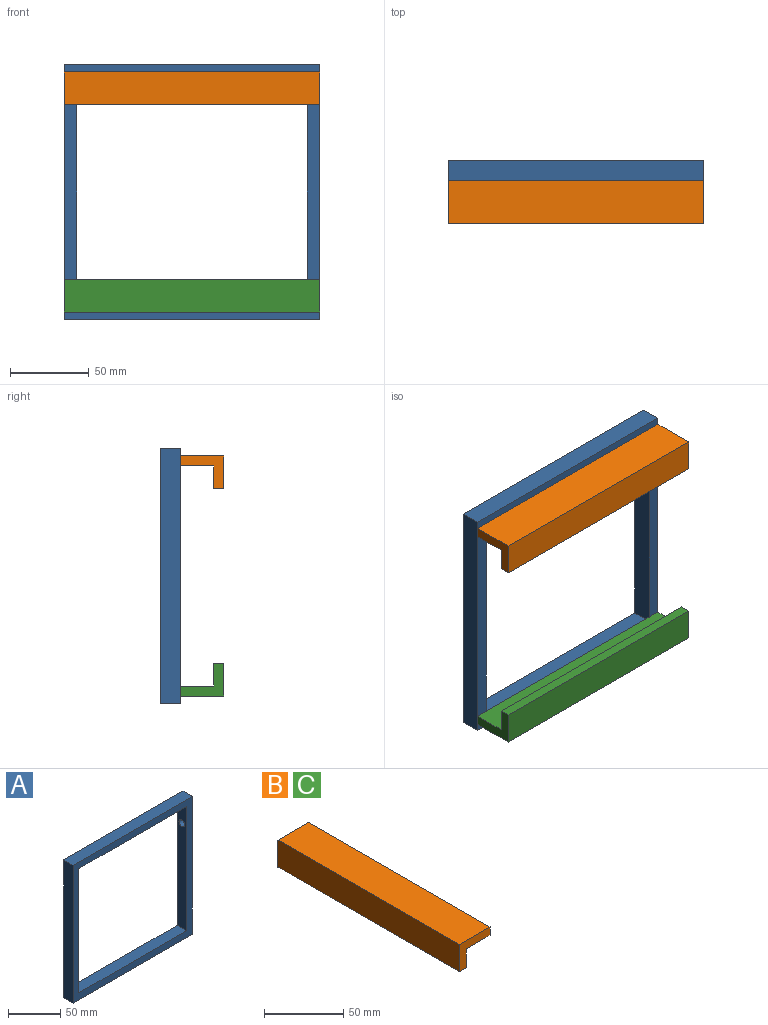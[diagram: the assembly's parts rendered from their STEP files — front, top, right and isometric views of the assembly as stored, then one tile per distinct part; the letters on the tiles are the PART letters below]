
ASSEMBLY  parts=3 mates=2
PART A: 11 faces, bbox 161.9x12.7x161.9 mm
  f0: plane 146.05x12.7mm, normal (0,0,-1), area 1854.8mm2, adj f1,f7,f8,f9
  f1: plane 146.05x12.7mm, normal (-1,0,0), area 1809.2mm2, adj f0,f2,f8,f9,f10
  f2: plane 146.05x12.7mm, normal (0,0,1), area 1854.8mm2, adj f1,f7,f8,f9
  f3: plane 161.93x12.7mm, normal (1,0,0), area 2010.8mm2, adj f4,f6,f8,f9,f10
  f4: plane 161.93x12.7mm, normal (0,0,1), area 2056.4mm2, adj f3,f5,f8,f9
  f5: plane 161.93x12.7mm, normal (-1,0,0), area 2056.4mm2, adj f4,f6,f8,f9
  f6: plane 161.93x12.7mm, normal (0,0,-1), area 2056.4mm2, adj f3,f5,f8,f9
  f7: plane 146.05x12.7mm, normal (1,0,0), area 1854.8mm2, adj f0,f2,f8,f9
  f8: plane 161.93x161.93mm, normal (0,-1,0), area 4889.1mm2, adj f0,f1,f2,f3,f4,f5,f6,f7
  f9: plane 161.93x161.93mm, normal (0,1,0), area 4889.1mm2, adj f0,f1,f2,f3,f4,f5,f6,f7
  f10: cylinder r=3.81mm len=7.94mm, axis (1,0,0), area 190mm2, adj f1,f3
PART B: 8 faces, bbox 27.4x161.9x20.9 mm
  f0: plane 161.93x27.45mm, normal (0,0,1), area 4444.6mm2, adj f1,f5,f6,f7
  f1: plane 161.93x20.9mm, normal (-1,0,0), area 3383.8mm2, adj f0,f2,f6,f7
  f2: plane 161.93x6.35mm, normal (0,0,-1), area 1028.2mm2, adj f1,f3,f6,f7
  f3: plane 161.93x14.55mm, normal (1,0,0), area 2355.6mm2, adj f2,f4,f6,f7
  f4: plane 161.93x21.1mm, normal (0,0,-1), area 3416.4mm2, adj f3,f5,f6,f7
  f5: plane 161.93x6.35mm, normal (1,0,0), area 1028.2mm2, adj f0,f4,f6,f7
  f6: plane 27.45x20.9mm, normal (0,-1,0), area 266.7mm2, adj f0,f1,f2,f3,f4,f5
  f7: plane 27.45x20.9mm, normal (0,1,0), area 266.7mm2, adj f0,f1,f2,f3,f4,f5
PART C: same geometry as B
PLACE A at identity fixed
PLACE B rot(axis=(0,0,1),90deg) t=(-80.96,-19.49,27.27)mm
PLACE C rot(axis=(-0.71,-0.71,0),180deg) t=(80.96,-19.49,-27.27)mm
MATE fastened A.f8 <-> B.f5  axis (0,-1,0) through (0,-12.7,73.03)mm
MATE fastened A.f8 <-> C.f5  axis (0,-1,0) through (0,-12.7,-73.03)mm
